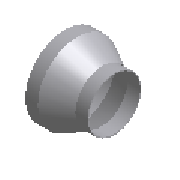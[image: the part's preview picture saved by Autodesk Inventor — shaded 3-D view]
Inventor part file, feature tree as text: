
AUTODESK INVENTOR PART (.ipt)
format: ipt  version: 2025 (Build 290162010, 162A)  size: 171,008 bytes
history: native  units: mm (DEFAULTED — no unit token found)
features: other x4, revolve x1
ambient origin geometry x8: Origin, YZ Plane, XZ Plane, XY Plane, X Axis, Y Axis, Z Axis, Center Point
bodies: Solid1 (feature_tree)
feature tree (5):
  revolve  "Revolution1"  [1 undecoded]
  other  "Work Axis1"
  other  "Work Point1"
  other  "Work Axis2"
  other  "Work Point2"
note: 1 required parameter value undecoded (feature->parameter linkage not recoverable at this tier; creation-order binding heuristic only, values carry confidence <= 0.55)
